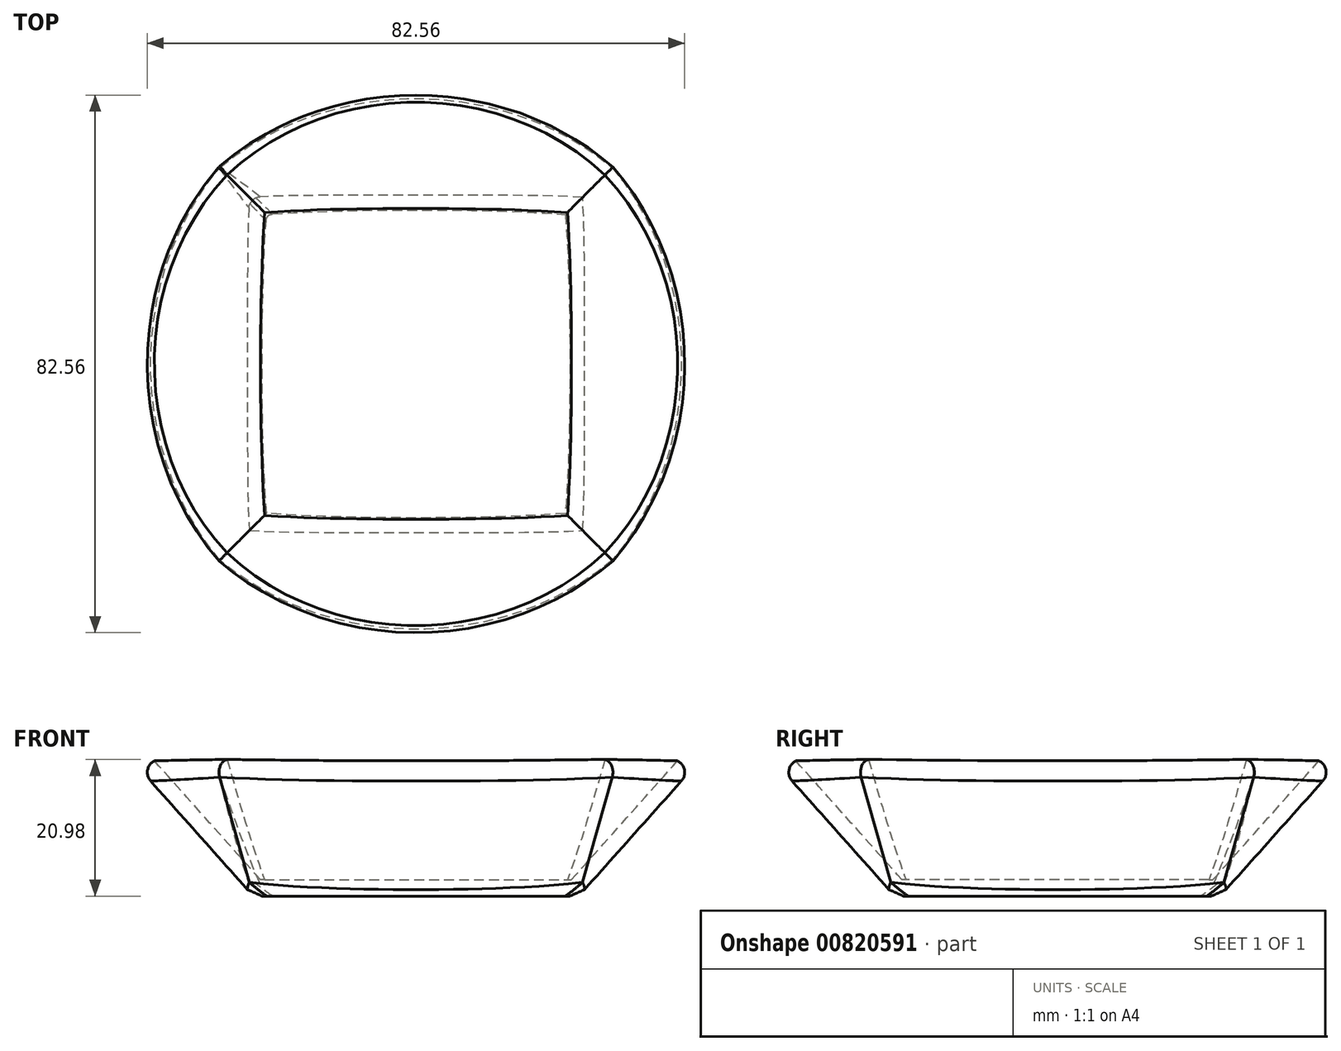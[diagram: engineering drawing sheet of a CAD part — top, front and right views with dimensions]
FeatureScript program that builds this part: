
annotation { "Feature Type Name" : "Feature", "Feature Type Description" : "" }
export const myFeature = defineFeature(function(context is Context, id is Id, definition is map)
    precondition{}
    {
        {
            var Q0;
            Q0=qCreatedBy(makeId("Top.planeOp"),FACE);
            var sketch = newSketch(context, id + "F0", { "sketchPlane" : qUnion([Q0])});
            skLineSegment(sketch, "E0.bottom", {"start": v(25, -25) * mm, "end": v(-25, -25) * mm});
            skLineSegment(sketch, "E0.top", {"start": v(25, 25) * mm, "end": v(-25, 25) * mm});
            skLineSegment(sketch, "E0.left", {"start": v(25, -25) * mm, "end": v(25, 25) * mm});
            skLineSegment(sketch, "E0.right", {"start": v(-25, -25) * mm, "end": v(-25, 25) * mm});
            skPoint(sketch, "E0.middle", {"position": v(0, 0) * mm});
            skSolve(sketch);
        }
        {
            var Q0;
            Q0=qCreatedBy(makeId("Top.planeOp"),FACE);
            cPlane(context, id + "F1", {"entities" : qUnion([Q0]), "cplaneType" : CPlaneType.OFFSET, "offset" : 21 * mm, "width" : 150 * mm, "height" : 150 * mm});
        }
        {
            var Q0;
            Q0=qCreatedBy(id+"F1.planeOp",FACE);
            var sketch = newSketch(context, id + "F2", { "sketchPlane" : qUnion([Q0])});
            skCircle(sketch, "E1", {"center": v(0, 0) * mm, "radius": 43.75 * mm});
            skSolve(sketch);
        }
        {
            var Q0;
            Q0=makeQuery(id+"F2.imprint","IMPRINT",FACE,{"disambiguationData":[TD([[makeQuery(id+"F2.imprint","IMPRINT",EDGE,{"derivedFrom":sQuery(id+"F2.wireOp",EDGE,"E1")}),1.0]])]});
            var Q1;
            Q1=makeQuery(id+"F0.imprint","IMPRINT",FACE,{"disambiguationData":[TD([[makeQuery(id+"F0.imprint","IMPRINT",EDGE,{"derivedFrom":sQuery(id+"F0.wireOp",EDGE,"E0.bottom")}),-1.0]])]});
            loft(context, id + "F3", {"sheetProfilesArray" : [{ "sheetProfileEntities" : qUnion([Q0]) }, { "sheetProfileEntities" : qUnion([Q1]) }]});
        }
        {
            var Q0;
            Q0=makeQuery(id+"F3.opLoft","CAP_FACE",FACE,{"disambiguationData":[OSD([makeQuery(id+"F2.imprint","IMPRINT",FACE,{"disambiguationData":[TD([[makeQuery(id+"F2.imprint","IMPRINT",EDGE,{"derivedFrom":sQuery(id+"F2.wireOp",EDGE,"E1")}),1.0]])]})])],"isStart":true});
            shell(context, id + "F4", {"entities" : qUnion([Q0]), "thickness" : 2.5 * mm});
        }
        {
            var Q0;
            Q0=makeQuery(id+"F3.opLoft","MID_CAP_EDGE",EDGE,{"disambiguationData":[OSD([sQuery(id+"F0.wireOp",EDGE,"E0.bottom"),sQuery(id+"F0.wireOp",EDGE,"E0.top"),sQuery(id+"F0.wireOp",EDGE,"E0.right"),sQuery(id+"F2.wireOp",EDGE,"E1")])],"capPos":0.0});
            var Q1;
            Q1=makeQuery(id+"F3.opLoft","MID_CAP_EDGE",EDGE,{"disambiguationData":[OSD([sQuery(id+"F0.wireOp",EDGE,"E0.bottom"),sQuery(id+"F0.wireOp",EDGE,"E0.left"),sQuery(id+"F0.wireOp",EDGE,"E0.right"),sQuery(id+"F2.wireOp",EDGE,"E1")])],"capPos":0.0});
            var Q2;
            Q2=makeQuery(id+"F3.opLoft","MID_CAP_EDGE",EDGE,{"disambiguationData":[OSD([sQuery(id+"F0.wireOp",EDGE,"E0.bottom"),sQuery(id+"F0.wireOp",EDGE,"E0.left"),sQuery(id+"F2.wireOp",EDGE,"E1")])],"capPos":0.0});
            var Q3;
            Q3=makeQuery(id+"F3.opLoft","MID_CAP_EDGE",EDGE,{"disambiguationData":[OSD([sQuery(id+"F0.wireOp",EDGE,"E0.bottom"),sQuery(id+"F0.wireOp",EDGE,"E0.top"),sQuery(id+"F0.wireOp",EDGE,"E0.left"),sQuery(id+"F0.wireOp",EDGE,"E0.right"),sQuery(id+"F2.wireOp",EDGE,"E1")])],"capPos":0.0});
            fillet(context, id + "F5", {"entities" : qUnion([Q0, Q1, Q2, Q3]), "radius" : 2 * mm, "tangentPropagation" : true, "allowEdgeOverflow" : false});
        }
        {
            var Q0;
            Q0=makeQuery(id+"F3.opLoft","MID_CAP_EDGE",EDGE,{"disambiguationData":[OSD([sQuery(id+"F0.wireOp",EDGE,"E0.bottom"),sQuery(id+"F0.wireOp",EDGE,"E0.top"),sQuery(id+"F0.wireOp",EDGE,"E0.right")])],"capPos":1.0});
            var Q1;
            Q1=makeQuery(id+"F3.opLoft","MID_CAP_EDGE",EDGE,{"disambiguationData":[OSD([sQuery(id+"F0.wireOp",EDGE,"E0.bottom"),sQuery(id+"F0.wireOp",EDGE,"E0.left"),sQuery(id+"F0.wireOp",EDGE,"E0.right")])],"capPos":1.0});
            var Q2;
            Q2=makeQuery(id+"F3.opLoft","MID_CAP_EDGE",EDGE,{"disambiguationData":[OSD([sQuery(id+"F0.wireOp",EDGE,"E0.bottom"),sQuery(id+"F0.wireOp",EDGE,"E0.top"),sQuery(id+"F0.wireOp",EDGE,"E0.left")])],"capPos":1.0});
            var Q3;
            Q3=makeQuery(id+"F3.opLoft","MID_CAP_EDGE",EDGE,{"disambiguationData":[OSD([sQuery(id+"F0.wireOp",EDGE,"E0.top"),sQuery(id+"F0.wireOp",EDGE,"E0.left"),sQuery(id+"F0.wireOp",EDGE,"E0.right")])],"capPos":1.0});
            chamfer(context, id + "F6", {"entities" : qUnion([Q0, Q1, Q2, Q3]), "width" : 3 * mm, "tangentPropagation" : true});
        }
        {
            var Q0;
            Q0=makeQuery(id+"F3.opLoft","SWEPT_EDGE",EDGE,{"disambiguationData":[OSD([sQuery(id+"F0.wireOp",EDGE,"E0.bottom"),sQuery(id+"F0.wireOp",EDGE,"E0.top"),sQuery(id+"F0.wireOp",EDGE,"E0.right"),sQuery(id+"F2.wireOp",EDGE,"E1")])]});
            var Q1;
            {var subQ0=sQuery(id+"F0.wireOp",EDGE,"E0.right");var subQ1=sQuery(id+"F0.wireOp",EDGE,"E0.top");Q1=makeQuery(id+"F6.opChamfer","BLEND_EDGE",EDGE,{"blendedFrom":[makeQuery(id+"F3.opLoft","MID_CAP_EDGE",EDGE,{"disambiguationData":[OSD([sQuery(id+"F0.wireOp",EDGE,"E0.bottom"),subQ1,subQ0])],"capPos":1.0}),makeQuery(id+"F3.opLoft","MID_CAP_EDGE",EDGE,{"disambiguationData":[OSD([subQ1,sQuery(id+"F0.wireOp",EDGE,"E0.left"),subQ0])],"capPos":1.0})],"blendedInto":[]});}
            fillet(context, id + "F7", {"entities" : qUnion([Q0, Q1]), "radius" : 2 * mm, "tangentPropagation" : true, "allowEdgeOverflow" : false});
        }
    });
